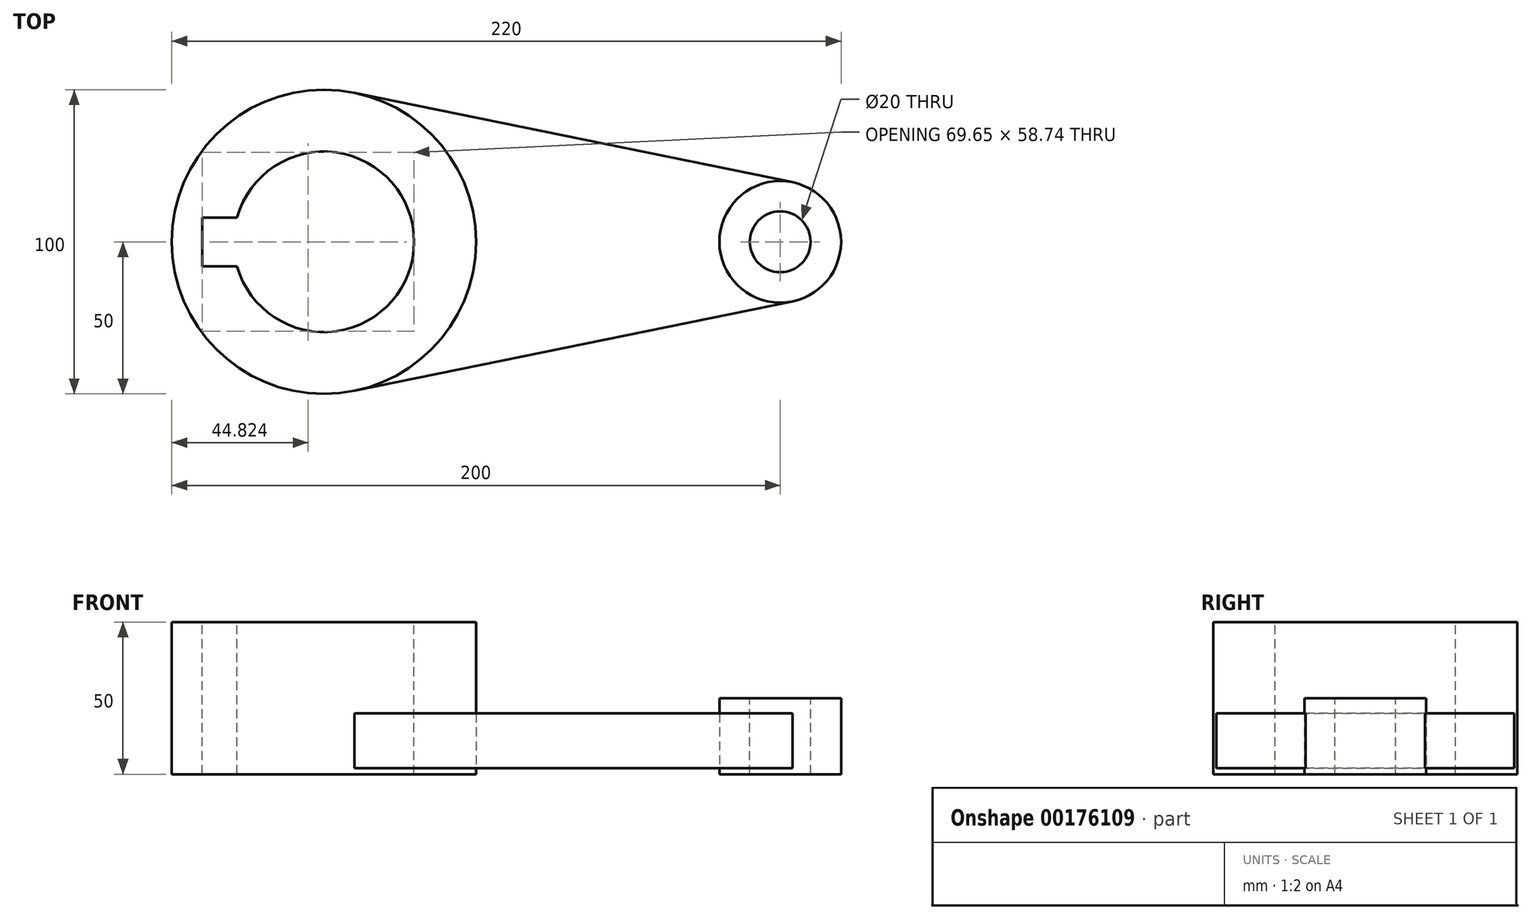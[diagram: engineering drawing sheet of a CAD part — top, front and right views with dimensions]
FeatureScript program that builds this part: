
annotation { "Feature Type Name" : "Feature", "Feature Type Description" : "" }
export const myFeature = defineFeature(function(context is Context, id is Id, definition is map)
    precondition{}
    {
        {
            var Q0;
            Q0=qCreatedBy(makeId("Top.planeOp"),FACE);
            var sketch = newSketch(context, id + "F0", { "sketchPlane" : qUnion([Q0])});
            skCircle(sketch, "E0", {"center": v(0, 0) * mm, "radius": 50 * mm});
            skCircle(sketch, "E1", {"center": v(150, 0) * mm, "radius": 20 * mm});
            skLineSegment(sketch, "E2", {"start": v(10, 48.99) * mm, "end": v(154, 19.6) * mm});
            skLineSegment(sketch, "E3", {"start": v(10, -48.99) * mm, "end": v(154, -19.6) * mm});
            skSolve(sketch);
        }
        {
            var Q0;
            {var subQ0=sQuery(id+"F0.wireOp",EDGE,"E0");var subQ1=makeQuery(id+"F0.imprint","INTERSECT",VERTEX,{"derivedFrom":[subQ0,sQuery(id+"F0.wireOp",EDGE,"E2")]});Q0=makeQuery(id+"F0.imprint","IMPRINT",FACE,{"disambiguationData":[TD([[makeQuery(id+"F0.imprint","IMPRINT",EDGE,{"disambiguationData":[TD([[subQ1,-1.0]])],"derivedFrom":subQ0}),1.0]])]});}
            extrude(context, id + "F1", {"entities" : qUnion([Q0]), "depth" : 50 * mm});
        }
        {
            var Q0;
            {var subQ0=sQuery(id+"F0.wireOp",EDGE,"E1");var subQ1=makeQuery(id+"F0.imprint","INTERSECT",VERTEX,{"derivedFrom":[subQ0,sQuery(id+"F0.wireOp",EDGE,"E2")]});Q0=makeQuery(id+"F0.imprint","IMPRINT",FACE,{"disambiguationData":[TD([[makeQuery(id+"F0.imprint","IMPRINT",EDGE,{"disambiguationData":[TD([[subQ1,-1.0]])],"derivedFrom":subQ0}),1.0]])]});}
            extrude(context, id + "F2", {"entities" : qUnion([Q0]), "depth" : 25 * mm});
        }
        {
            var Q0;
            {var subQ0=sQuery(id+"F0.wireOp",EDGE,"E2");Q0=makeQuery(id+"F0.imprint","IMPRINT",FACE,{"disambiguationData":[TD([[makeQuery(id+"F0.imprint","IMPRINT",EDGE,{"derivedFrom":subQ0}),-1.0]])]});}
            extrude(context, id + "F3", {"entities" : qUnion([Q0]), "depth" : 20 * mm});
        }
        {
            var Q0;
            {var subQ0=sQuery(id+"F0.wireOp",EDGE,"E2");Q0=makeQuery(id+"F0.imprint","IMPRINT",FACE,{"disambiguationData":[TD([[makeQuery(id+"F0.imprint","IMPRINT",EDGE,{"derivedFrom":subQ0}),-1.0]])]});}
            extrude(context, id + "F4", {"entities" : qUnion([Q0]), "operationType" : NewBodyOperationType.REMOVE, "depth" : 2 * mm});
        }
        {
            var Q0;
            Q0=makeQuery(id+"F1.opExtrude","CAP_FACE",FACE,{"disambiguationData":[OSD([sQuery(id+"F0.wireOp",EDGE,"E0")])],"isStart":false});
            var sketch = newSketch(context, id + "F5", { "sketchPlane" : qUnion([Q0])});
            skCircle(sketch, "E4", {"center": v(0, 0) * mm, "radius": 29.65 * mm});
            skSolve(sketch);
        }
        {
            var Q0;
            Q0 = qSketchRegion(id + "F5", true);
            extrude(context, id + "F6", {"entities" : qUnion([Q0]), "operationType" : NewBodyOperationType.REMOVE, "oppositeDirection" : true, "depth" : 130 * mm});
        }
        {
            var Q0;
            Q0=makeQuery(id+"F1.opExtrude","CAP_FACE",FACE,{"disambiguationData":[OSD([sQuery(id+"F0.wireOp",EDGE,"E0")])],"isStart":false});
            var sketch = newSketch(context, id + "F7", { "sketchPlane" : qUnion([Q0])});
            skLineSegment(sketch, "E5.bottom", {"start": v(-40, 8) * mm, "end": v(-17.9, 8) * mm});
            skLineSegment(sketch, "E5.top", {"start": v(-40, -8) * mm, "end": v(-17.9, -8) * mm});
            skLineSegment(sketch, "E5.left", {"start": v(-40, 8) * mm, "end": v(-40, -8) * mm});
            skLineSegment(sketch, "E5.right", {"start": v(-17.9, 8) * mm, "end": v(-17.9, -8) * mm});
            skSolve(sketch);
        }
        {
            var Q0;
            Q0 = qSketchRegion(id + "F7", true);
            extrude(context, id + "F8", {"entities" : qUnion([Q0]), "operationType" : NewBodyOperationType.REMOVE, "oppositeDirection" : true, "depth" : 118 * mm});
        }
        {
            var Q0;
            Q0=makeQuery(id+"F2.opExtrude","CAP_FACE",FACE,{"disambiguationData":[OSD([sQuery(id+"F0.wireOp",EDGE,"E1")])],"isStart":false});
            var sketch = newSketch(context, id + "F9", { "sketchPlane" : qUnion([Q0])});
            skCircle(sketch, "E6", {"center": v(150, 0) * mm, "radius": 10 * mm});
            skSolve(sketch);
        }
        {
            var Q0;
            Q0 = qSketchRegion(id + "F9", true);
            extrude(context, id + "F10", {"entities" : qUnion([Q0]), "operationType" : NewBodyOperationType.REMOVE, "oppositeDirection" : true, "depth" : 52 * mm});
        }
    });
